# Revit family: 6. Секция фреонового охлаждения ANR C2
name_source: partatom
category: Оборудование
revit_build: Autodesk Revit 2016 (Build: 20151209_0715(x64)
units: mm (PartAtom-declared; Revit-internal decimal feet)

## family parameters
Всегда вертикально = Да
На основе рабочей плоскости = Нет
Общий = Нет
При загрузке вырезать с полостями = Нет
Размер круглого соединителя = Использовать диаметр
Тип детали = Нормальный
Точка расчета площади = Нет

## types (20) — shared parameters
h = 130 мм
Д = 575 мм
Д1 = 555 мм
Е = 85 мм
Единица измерения = шт.
Завод изготовитель = KORF
Ключевая пометка = Вентиляция
Наименование и тех.хар-ка = Секция фреонового охлаждения
Раздел = ОВ
Размер В = 85 мм
Синий = Синий
высота ножек = 120 мм

## per-type parameters (varying)
| type | А | А1 | Б | Б1 | Высота | Г | Дгаз | Джид | Ж | З | Заправочный объем, л | И | И1 | Материал | Середина | Ширина |
| ANR 6 C2.3 | 1100 мм | 1080 мм | 1100 мм | 1080 мм | 1025 мм | 530 мм | 28 мм | 22 мм | 45 мм | 45 мм | 7 м³ | 135 мм | 125 мм | Сталь серая | 670 мм | 1025 мм |
| ANR 6 C2.4 | 1100 мм | 1080 мм | 1100 мм | 1080 мм | 1025 мм | 530 мм | 35 мм | 22 мм | 45 мм | 45 мм | 9 м³ | 135 мм | 125 мм | RAL 0000 Серый металл | 670 мм | 1025 мм |
| ANR 7 C2.3 | 1100 мм | 1080 мм | 1320 мм | 1300 мм | 1245 мм | 790 мм | 35 мм | 22 мм | 45 мм | 45 мм | 9.2 м³ | 115 мм | 105 мм | Сталь серая | 780 мм | 1025 мм |
| ANR 7 C2.4 | 1100 мм | 1080 мм | 1320 мм | 1300 мм | 1245 мм | 790 мм | 35 мм | 22 мм | 45 мм | 45 мм | 11.9 м³ | 115 мм | 105 мм | Сталь серая | 780 мм | 1025 мм |
| ANR 8 C2.3 | 1320 мм | 1300 мм | 1320 мм | 1300 мм | 1245 мм | 790 мм | 35 мм | 22 мм | 45 мм | 45 мм | 11.2 м³ | 115 мм | 105 мм | Сталь серая | 780 мм | 1245 мм |
| ANR 8 C2.4 | 1320 мм | 1300 мм | 1320 мм | 1300 мм | 1245 мм | 790 мм | 35 мм | 22 мм | 45 мм | 45 мм | 15.1 м³ | 115 мм | 105 мм | Сталь серая | 780 мм | 1245 мм |
| ANR 12 C2.3 | 1435 мм | 1415 мм | 1435 мм | 1415 мм | 1360 мм | 905 мм | 35 мм | 22 мм | 45 мм | 45 мм | 13.3 м³ | 115 мм | 105 мм | Сталь серая | 838 мм | 1360 мм |
| ANR 12 C2.4 | 1435 мм | 1415 мм | 1435 мм | 1415 мм | 1360 мм | 905 мм | 35 мм | 22 мм | 45 мм | 45 мм | 17.2 м³ | 115 мм | 105 мм | Сталь серая | 838 мм | 1360 мм |
| ANR 20 C2.3 | 1660 мм | 1640 мм | 1660 мм | 1640 мм | 1585 мм | 1130 мм | 42 мм | 28 мм | 50 мм | 58 мм | 24.1 м³ | 115 мм | 105 мм | Сталь серая | 950 мм | 1585 мм |
| ANR 20 C2.4 | 1660 мм | 1640 мм | 1660 мм | 1640 мм | 1585 мм | 1130 мм | 42 мм | 28 мм | 50 мм | 58 мм | 32.7 м³ | 115 мм | 105 мм | Сталь серая | 950 мм | 1585 мм |
| ANR 25 C2.3 | 2045 мм | 2025 мм | 2045 мм | 2025 мм | 1970 мм | 1515 мм | 42 мм | 28 мм | 50 мм | 68 мм | 37.8 м³ | 115 мм | 105 мм | Сталь серая | 1143 мм | 1970 мм |
| ANR 25 C2.4 | 2045 мм | 2025 мм | 2045 мм | 2025 мм | 1970 мм | 1515 мм | 42 мм | 28 мм | 50 мм | 68 мм | 53.1 м³ | 115 мм | 105 мм | Сталь серая | 1143 мм | 1970 мм |
| ANR 30 C2.3 | 2485 мм | 2465 мм | 2045 мм | 2025 мм | 1970 мм | 1515 мм | 42 мм | 28 мм | 70 мм | 30 мм | 52 м³ | 115 мм | 105 мм | Сталь серая | 1143 мм | 2410 мм |
| ANR 30 C2.4 | 2485 мм | 2465 мм | 2045 мм | 2025 мм | 1970 мм | 1515 мм | 42 мм | 28 мм | 70 мм | 30 мм | 66.7 м³ | 115 мм | 105 мм | Сталь серая | 1143 мм | 2410 мм |
| ANR 35 C2.3 | 2485 мм | 2465 мм | 2485 мм | 2465 мм | 2410 мм | 1955 мм | 54 мм | 35 мм | 80 мм | 35 мм | 64.4 м³ | 115 мм | 105 мм | Сталь серая | 1363 мм | 2410 мм |
| ANR 35 C2.4 | 2485 мм | 2465 мм | 2485 мм | 2465 мм | 2410 мм | 1955 мм | 54 мм | 35 мм | 80 мм | 35 мм | 86.3 м³ | 115 мм | 105 мм | Сталь серая | 1363 мм | 2410 мм |
| ANR 40 C2.3 | 3320 мм | 3300 мм | 3320 мм | 3300 мм | 3245 мм | 1130 мм | 54 мм | 0 мм | 70 мм | 30 мм | 96 м³ | 115 мм | 105 мм | Сталь серая | 1780 мм | 3245 мм |
| ANR 40 C2.4 | 3320 мм | 3300 мм | 3320 мм | 3300 мм | 3245 мм | 1130 мм | 54 мм | 0 мм | 70 мм | 30 мм | 130 м³ | 115 мм | 105 мм | Сталь серая | 1780 мм | 3245 мм |
| ANR 45 C2.3 | 3320 мм | 3300 мм | 4090 мм | 4070 мм | 4015 мм | 1515 мм | 54 мм | 0 мм | 80 мм | 36 мм | 152 м³ | 115 мм | 105 мм | Сталь серая | 2165 мм | 3245 мм |
| ANR 45 C2.4 | 3320 мм | 3300 мм | 4090 мм | 4070 мм | 4015 мм | 1515 мм | 54 мм | 0 мм | 80 мм | 36 мм | 212 м³ | 115 мм | 105 мм | Сталь серая | 2165 мм | 3245 мм |

note: column(s) folded — value = type name in every type: Тип, марка, обозначение
